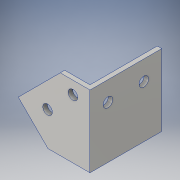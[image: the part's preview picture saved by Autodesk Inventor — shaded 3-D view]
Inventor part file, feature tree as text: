
AUTODESK INVENTOR PART (.ipt)
format: ipt  version: 2016 (Build 200138000, 138)  size: 152,576 bytes
history: native  units: in
note: dims shown in document units (in); Inventor stores cm internally (conversion verified against a paired STEP export)
features: extrude x4, sketch x4
ambient origin geometry x8: Origin, YZ Plane, XZ Plane, XY Plane, X Axis, Y Axis, Z Axis, Center Point
bodies: Solid1 (feature_tree)
feature tree (8):
  extrude  "Extrusion1"  Depth=2.0in
  extrude  "Extrusion2"  TaperAngle=135.0deg  [1 undecoded]
  extrude  "Extrusion3"  Depth=0.125in
  extrude  "Extrusion4"  Depth=0.125in
  sketch  "Sketch1"  dims[d0=2.0in d2=2.0in]
  sketch  "Sketch2"  dims[d3=2.0in d4=135.0deg]
  sketch  "Sketch3"  dims[d5=0.125in d6=0.0in d7=0.125in]
  sketch  "Sketch4"  dims[d8=2.0in d9=0.0in d10=0.2656in d11=0.2656in d12=0.546in d13=0.546in d14=0.5in d15=1.0in d16=0.125in d17=0.0in d18=0.656in d19=0.5in d20=0.5in d21=0.2656in d22=1.0in d23=0.125in d24=0.0in d25=0.4755in d26=1.1826in d27=0.3542in d28=1.0613in d29=0.9387in]
note: 1 required parameter value undecoded (feature->parameter linkage not recoverable at this tier; creation-order binding heuristic only, values carry confidence <= 0.55)
